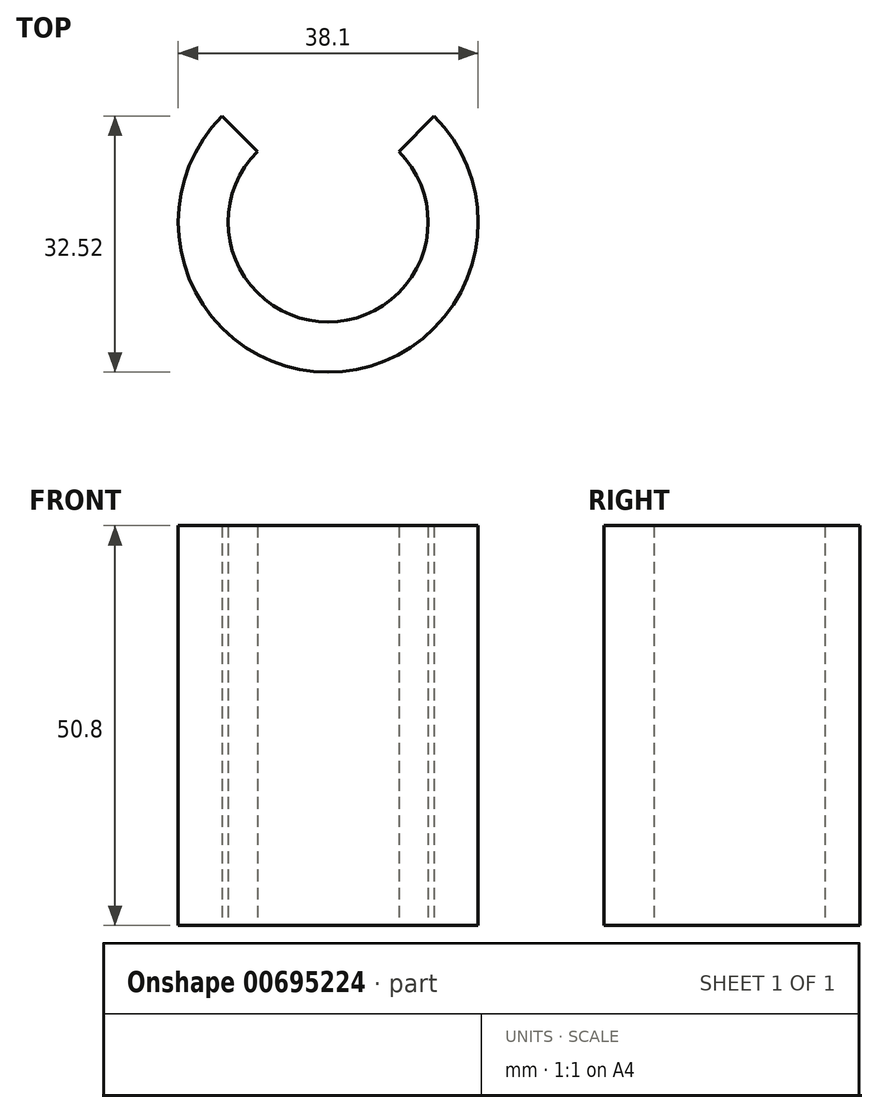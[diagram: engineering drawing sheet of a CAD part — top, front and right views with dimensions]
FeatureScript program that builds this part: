
annotation { "Feature Type Name" : "Feature", "Feature Type Description" : "" }
export const myFeature = defineFeature(function(context is Context, id is Id, definition is map)
    precondition{}
    {
        {
            var Q0;
            Q0=qCreatedBy(makeId("Top.planeOp"),FACE);
            var sketch = newSketch(context, id + "F0", { "sketchPlane" : qUnion([Q0])});
            skCircle(sketch, "E0", {"center": v(0, 0) * mm, "radius": 12.7 * mm});
            skArc(sketch, "E1", {"start": v(-13.47, 13.47) * mm, "mid": v(0, -19.05) * mm, "end": v(13.47, 13.47) * mm});
            skLineSegment(sketch, "E2", {"start": v(0, 0) * mm, "end": v(0, 19.05) * mm});
            skLineSegment(sketch, "E3", {"start": v(0, 0) * mm, "end": v(13.47, 13.47) * mm});
            skLineSegment(sketch, "E4.MirrorCS", {"start": v(0, 0) * mm, "end": v(-13.47, 13.47) * mm});
            skSolve(sketch);
        }
        {
            var Q0;
            {var subQ5=sQuery(id+"F0.wireOp",EDGE,"E1");Q0=makeQuery(id+"F0.imprint","IMPRINT",FACE,{"disambiguationData":[TD([[makeQuery(id+"F0.imprint","IMPRINT",EDGE,{"derivedFrom":subQ5}),1.0]])]});}
            extrude(context, id + "F1", {"entities" : qUnion([Q0]), "depth" : 50.8 * mm, "offsetDistance" : 25.4 * mm});
        }
    });
